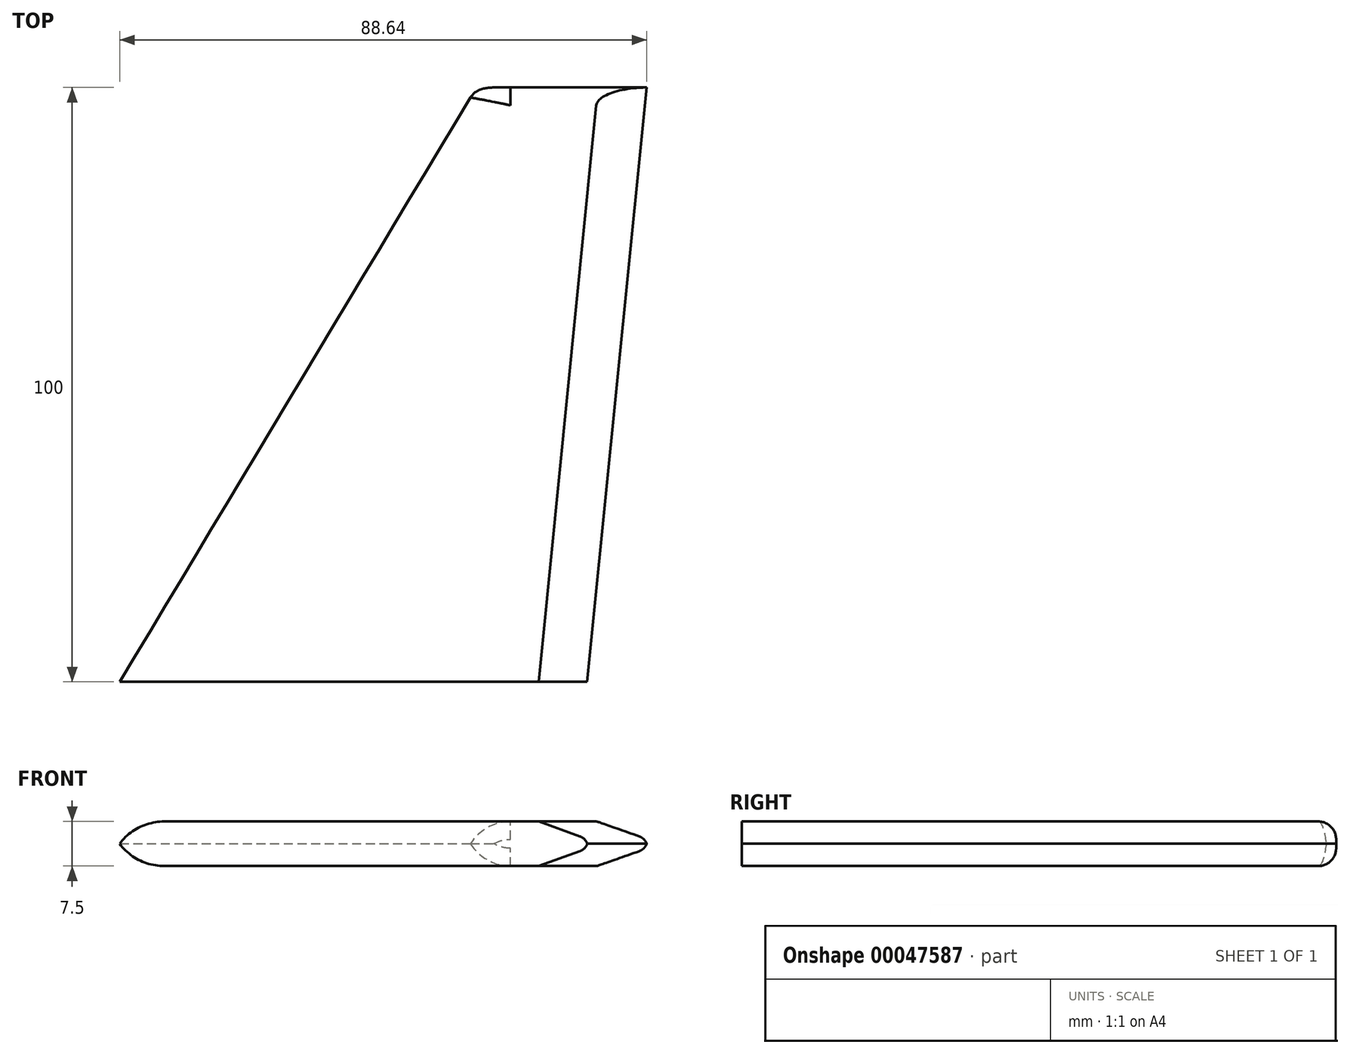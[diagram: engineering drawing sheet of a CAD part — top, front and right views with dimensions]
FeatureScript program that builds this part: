
annotation { "Feature Type Name" : "Feature", "Feature Type Description" : "" }
export const myFeature = defineFeature(function(context is Context, id is Id, definition is map)
    precondition{}
    {
        {
            var Q0;
            Q0=qCreatedBy(makeId("Top.planeOp"),FACE);
            var sketch = newSketch(context, id + "F0", { "sketchPlane" : qUnion([Q0])});
            skLineSegment(sketch, "E0.bottom", {"start": v(-34.01, 60.27) * mm, "end": v(-14.01, 60.27) * mm});
            skLineSegment(sketch, "E0.top", {"start": v(-34.01, -39.73) * mm, "end": v(-14.01, -39.73) * mm});
            skLineSegment(sketch, "E0.left", {"start": v(-34.01, 60.27) * mm, "end": v(-34.01, -39.73) * mm});
            skLineSegment(sketch, "E0.right", {"start": v(-14.01, 60.27) * mm, "end": v(-14.01, -39.73) * mm});
            skLineSegment(sketch, "E1", {"start": v(-14.01, 60.27) * mm, "end": v(-4.01, 60.27) * mm});
            skLineSegment(sketch, "E2", {"start": v(-4.01, 60.27) * mm, "end": v(-14.01, -39.73) * mm});
            skLineSegment(sketch, "E3", {"start": v(-34.01, -39.73) * mm, "end": v(-94.01, -39.73) * mm});
            skLineSegment(sketch, "E4", {"start": v(-94.01, -39.73) * mm, "end": v(-34.01, 60.27) * mm});
            skSolve(sketch);
        }
        {
            var Q0;
            Q0=makeQuery(id+"F0.imprint","IMPRINT",FACE,{"disambiguationData":[TD([[makeQuery(id+"F0.imprint","IMPRINT",EDGE,{"derivedFrom":sQuery(id+"F0.wireOp",EDGE,"E0.left")}),-1.0]])]});
            var Q1;
            Q1=makeQuery(id+"F0.imprint","IMPRINT",FACE,{"disambiguationData":[TD([[makeQuery(id+"F0.imprint","IMPRINT",EDGE,{"derivedFrom":sQuery(id+"F0.wireOp",EDGE,"E0.bottom")}),-1.0]])]});
            var Q2;
            Q2=makeQuery(id+"F0.imprint","IMPRINT",FACE,{"disambiguationData":[TD([[makeQuery(id+"F0.imprint","IMPRINT",EDGE,{"derivedFrom":sQuery(id+"F0.wireOp",EDGE,"E0.right")}),1.0]])]});
            extrude(context, id + "F1", {"entities" : qUnion([Q0, Q1, Q2]), "depth" : 7.5 * mm});
        }
        {
            var Q0;
            Q0=makeQuery(id+"F1.opExtrude","CAP_EDGE",EDGE,{"disambiguationData":[OSD([sQuery(id+"F0.wireOp",EDGE,"E4")])],"isStart":false});
            var Q1;
            Q1=makeQuery(id+"F1.opExtrude","CAP_EDGE",EDGE,{"disambiguationData":[OSD([sQuery(id+"F0.wireOp",EDGE,"E4")])],"isStart":true});
            fillet(context, id + "F2", {"entities" : qUnion([Q0, Q1]), "radius" : 7.5 * mm, "rho" : .4, "crossSection" : FilletCrossSection.CONIC, "allowEdgeOverflow" : false});
        }
        {
            var Q0;
            Q0=makeQuery(id+"F1.opExtrude","CAP_EDGE",EDGE,{"disambiguationData":[OSD([sQuery(id+"F0.wireOp",EDGE,"E2")])],"isStart":false});
            var Q1;
            Q1=makeQuery(id+"F1.opExtrude","CAP_EDGE",EDGE,{"disambiguationData":[OSD([sQuery(id+"F0.wireOp",EDGE,"E2")])],"isStart":true});
            chamfer(context, id + "F3", {"entities" : qUnion([Q0, Q1]), "chamferType" : ChamferType.OFFSET_ANGLE, "width" : 3 * mm, "oppositeDirection" : false, "angle" : 70 * degree, "tangentPropagation" : true});
        }
        {
            var Q0;
            {var subQ0=sQuery(id+"F0.wireOp",EDGE,"E2");Q0=makeQuery(id+"F3.opChamfer","BLEND_EDGE",EDGE,{"blendedFrom":[makeQuery(id+"F1.opExtrude","CAP_EDGE",EDGE,{"disambiguationData":[OSD([subQ0])],"isStart":false}),makeQuery(id+"F1.opExtrude","SWEPT_FACE",FACE,{"disambiguationData":[OSD([subQ0])]})],"blendedInto":[makeQuery(id+"F1.opExtrude","SWEPT_FACE",FACE,{"disambiguationData":[OSD([subQ0])]})]});}
            var Q1;
            {var subQ0=sQuery(id+"F0.wireOp",EDGE,"E2");Q1=makeQuery(id+"F3.opChamfer","BLEND_EDGE",EDGE,{"blendedFrom":[makeQuery(id+"F1.opExtrude","CAP_EDGE",EDGE,{"disambiguationData":[OSD([subQ0])],"isStart":true}),makeQuery(id+"F1.opExtrude","SWEPT_FACE",FACE,{"disambiguationData":[OSD([subQ0])]})],"blendedInto":[makeQuery(id+"F1.opExtrude","SWEPT_FACE",FACE,{"disambiguationData":[OSD([subQ0])]})]});}
            fillet(context, id + "F4", {"entities" : qUnion([Q0, Q1]), "radius" : 2 * mm, "tangentPropagation" : true, "allowEdgeOverflow" : false});
        }
        {
            var Q0;
            Q0=makeQuery(id+"F1.opExtrude","CAP_EDGE",EDGE,{"disambiguationData":[OSD([sQuery(id+"F0.wireOp",EDGE,"E0.bottom"),sQuery(id+"F0.wireOp",EDGE,"E1")])],"isStart":true});
            var Q1;
            Q1=makeQuery(id+"F1.opExtrude","CAP_EDGE",EDGE,{"disambiguationData":[OSD([sQuery(id+"F0.wireOp",EDGE,"E0.bottom"),sQuery(id+"F0.wireOp",EDGE,"E1")])],"isStart":false});
            fillet(context, id + "F5", {"entities" : qUnion([Q0, Q1]), "radius" : 3 * mm, "tangentPropagation" : true, "allowEdgeOverflow" : false});
        }
    });
